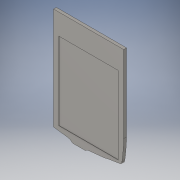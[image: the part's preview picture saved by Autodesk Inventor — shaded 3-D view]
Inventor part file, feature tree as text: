
AUTODESK INVENTOR PART (.ipt)
format: ipt  version: 2019 (Build 230136000, 136)  size: 138,752 bytes
history: mixed  units: in
note: dims shown in document units (in); Inventor stores cm internally (conversion verified against a paired STEP export)
features: extrude x2, sketch x2, other x1, projected_geometry x1, imported_body x1
ambient origin geometry x8: Origin, YZ Plane, XZ Plane, XY Plane, X Axis, Y Axis, Z Axis, Center Point
bodies: Solid1 (imported_parasolid)
feature tree (7):
  other  "base plate"
  extrude  "Wyciągnięcie proste1"  Depth=1.1811in TaperAngle=0.0deg
  extrude  "Wyciągnięcie proste2"  Depth=1.1811in TaperAngle=0.0deg
  sketch  "Szkic2"
  projected_geometry  "Pętla rzutowana1"
  sketch  "Szkic3"
  imported_body  NMx_Import_Brep_tag  [imported B-rep: ~6 faces, bbox_mm=None]
